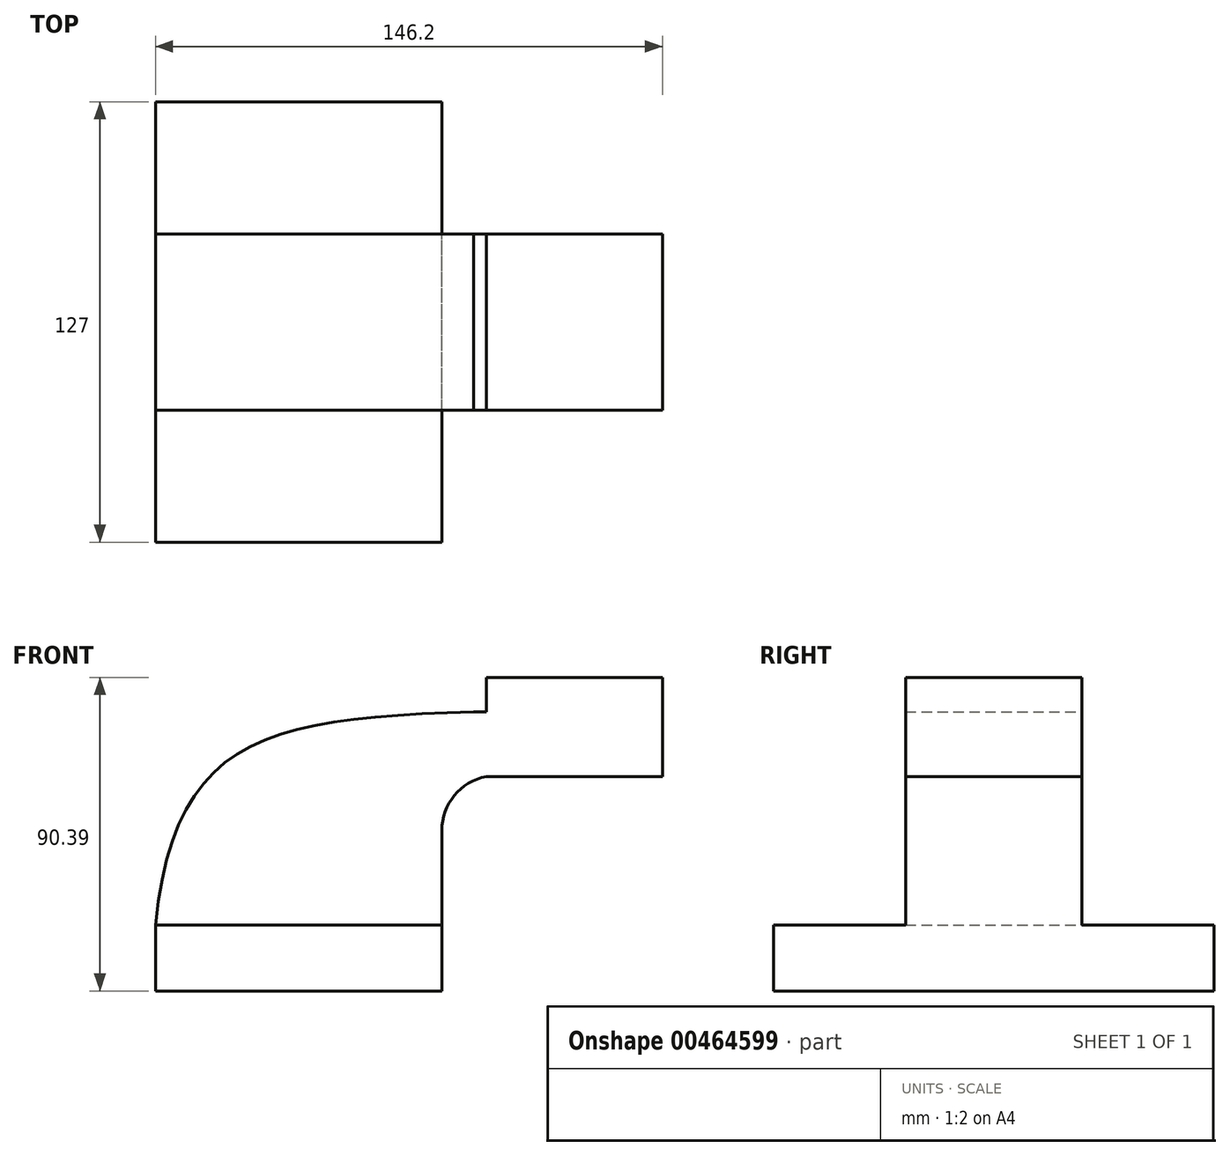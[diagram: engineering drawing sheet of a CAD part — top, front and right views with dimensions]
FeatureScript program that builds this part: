
annotation { "Feature Type Name" : "Feature", "Feature Type Description" : "" }
export const myFeature = defineFeature(function(context is Context, id is Id, definition is map)
    precondition{}
    {
        {
            var Q0;
            Q0=qCreatedBy(makeId("Front.planeOp"),FACE);
            var sketch = newSketch(context, id + "F0", { "sketchPlane" : qUnion([Q0])});
            skLineSegment(sketch, "E0.bottom", {"start": v(41.27, 9.53) * mm, "end": v(-41.28, 9.53) * mm});
            skLineSegment(sketch, "E0.top", {"start": v(41.28, -9.52) * mm, "end": v(-41.27, -9.52) * mm});
            skLineSegment(sketch, "E0.left", {"start": v(41.27, 9.53) * mm, "end": v(41.28, -9.52) * mm});
            skLineSegment(sketch, "E0.right", {"start": v(-41.28, 9.53) * mm, "end": v(-41.27, -9.52) * mm});
            skPoint(sketch, "E0.middle", {"position": v(0, 0) * mm});
            skLineSegment(sketch, "E1.bottom", {"start": v(104.92, 80.86) * mm, "end": v(54.12, 80.86) * mm});
            skLineSegment(sketch, "E1.top", {"start": v(104.92, 52.28) * mm, "end": v(54.12, 52.28) * mm});
            skLineSegment(sketch, "E1.left", {"start": v(104.92, 80.86) * mm, "end": v(104.92, 52.28) * mm});
            skLineSegment(sketch, "E1.right", {"start": v(54.12, 80.86) * mm, "end": v(54.12, 52.28) * mm});
            skPoint(sketch, "E1.middle", {"position": v(79.52, 66.57) * mm});
            skLineSegment(sketch, "E2", {"start": v(41.27, 9.53) * mm, "end": v(41.27, 36.7) * mm});
            skArc(sketch, "E3", {"start": v(41.27, 36.7) * mm, "mid": v(44.9, 46.8) * mm, "end": v(54.12, 52.28) * mm});
            skArc(sketch, "E4.0", {"start": v(22.22, 36.7) * mm, "mid": v(30.2, 58.91) * mm, "end": v(50.48, 70.98) * mm});
            skLineSegment(sketch, "E4.1", {"start": v(22.22, 9.53) * mm, "end": v(22.22, 36.7) * mm});
            skLineSegment(sketch, "E5", {"start": v(50.48, 70.98) * mm, "end": v(64.49, 70.98) * mm});
            skLineSegment(sketch, "E6", {"start": v(54.12, 52.28) * mm, "end": v(64.49, 52.28) * mm});
            skLineSegment(sketch, "E7", {"start": v(64.49, 70.98) * mm, "end": v(64.49, 52.28) * mm});
            skFitSpline(sketch, "E8", {"points": [v(-41.28, 9.52) * mm, v(50.48, 70.98) * mm], "startDerivative": vector(16.9, 162.81) * mm, "endDerivative": vector(180.35, 5.79) * mm});
            skSolve(sketch);
        }
        {
            var Q0;
            Q0=makeQuery(id+"F0.imprint","IMPRINT",FACE,{"disambiguationData":[TD([[makeQuery(id+"F0.imprint","IMPRINT",EDGE,{"derivedFrom":sQuery(id+"F0.wireOp",EDGE,"E0.top")}),-1.0]])]});
            extrude(context, id + "F1", {"entities" : qUnion([Q0]), "endBound" : BoundingType.SYMMETRIC, "depth" : 127 * mm});
        }
        {
            var Q0;
            Q0 = qSketchRegion(id + "F0", true);
            extrude(context, id + "F2", {"entities" : qUnion([Q0]), "operationType" : NewBodyOperationType.ADD, "endBound" : BoundingType.SYMMETRIC, "depth" : 50.8 * mm});
        }
    });
